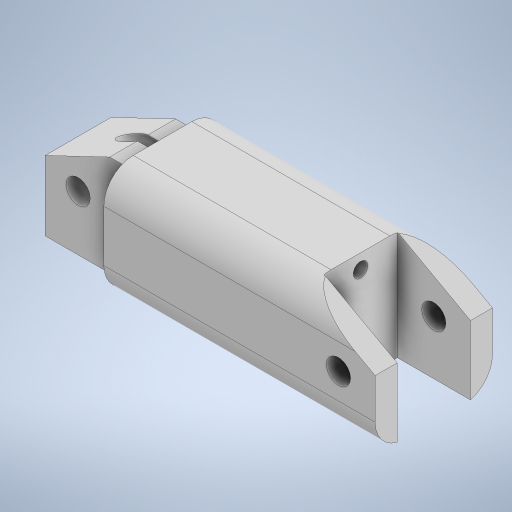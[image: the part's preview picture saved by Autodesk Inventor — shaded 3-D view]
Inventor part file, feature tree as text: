
AUTODESK INVENTOR PART (.ipt)
format: ipt  version: 2024 (Build 280153000, 153)  size: 504,832 bytes
history: native  units: mm
features: sketch x25, extrude x20, chamfer x3, move_body x3, plane x2, split x2, boolean_combine x2, fillet x1
ambient origin geometry x8: Origin, YZ Plane, XZ Plane, XY Plane, X Axis, Y Axis, Z Axis, Center Point
bodies: Solid1 (feature_tree), Solid2 (feature_tree), Solid3 (feature_tree), Solid4 (feature_tree), Solid5 (feature_tree)
feature tree (58):
  extrude  "Extrusion1"  Depth=16.0mm
  sketch  "Sketch2"  dims[d2=15.0mm d3=0.0mm d4=10.0mm]
  extrude  "Extrusion2"  Depth=10.0mm
  chamfer  "Chamfer1"  Distance=21.25mm
  extrude  "Extrusion3"  Depth=10.0mm TaperAngle=0.0deg
  extrude  "Extrusion4"  Depth=11.5mm TaperAngle=0.0deg
  extrude  "Extrusion5"  Depth=1.0mm TaperAngle=0.0deg
  chamfer  "Chamfer2"  Distance=6.0mm Angle=45.0deg
  sketch  "Sketch6"  dims[d14=7.0mm d15=11.5mm d16=0.0mm]
  extrude  "Extrusion6"  Depth=9.0mm
  extrude  "Extrusion7"  Depth=11.5mm TaperAngle=0.0deg
  chamfer  "Chamfer3"  Distance=11.5mm Angle=45.0deg
  sketch  "Sketch9"  dims[d26=3.3mm d27=45.25mm d28=0.0mm d29=11.5mm d30=5.5mm d31=45.0deg]
  extrude  "Extrusion8"  Depth=65.75mm TaperAngle=0.0deg
  extrude  "Extrusion9"  Depth=9.0mm TaperAngle=0.0deg
  extrude  "Extrusion10"  Depth=13.0mm TaperAngle=0.0deg
  sketch  "Sketch13"  dims[d43=24.0mm d44=21.0mm d45=0.0mm]
  extrude  "Extrusion11"  Depth=21.0mm TaperAngle=0.0deg
  extrude  "Extrusion12"  TaperAngle=0.0deg  [1 undecoded]
  extrude  "Extrusion13"  Depth=6.0mm TaperAngle=0.0deg
  plane  "Work Plane1"
  split  "Split1"
  move_body  "Move Body1"
  extrude  "Extrusion14"  Depth=0.5mm TaperAngle=0.0deg
  move_body  "Move Body2"
  fillet  "Fillet1"  Radius=10.0mm
  extrude  "Extrusion15"  Depth=10.0mm TaperAngle=0.0deg
  sketch  "Sketch19"  dims[d71=29.5mm d72=0.0mm d73=13.75mm]
  sketch  "Sketch20"  dims[d74=26.0mm d75=0.0mm d76=-5.0mm d77=0.0mm d78=0.0mm]
  extrude  "Extrusion16"  Depth=1.0mm
  extrude  "Extrusion18"  Depth=13.75mm
  extrude  "Extrusion19"  TaperAngle=0.0deg  [1 undecoded]
  sketch  "Sketch23"
  sketch  "Sketch24"
  extrude  "Extrusion20"  [1 undecoded]
  plane  "Work Plane2"
  boolean_combine  "Combine1"
  split  "Split2"
  extrude  "Extrusion21"  [1 undecoded]
  move_body  "Move Body3"
  boolean_combine  "Combine2"
  sketch  "Sketch1"  dims[d0=36.0mm d1=16.0mm]
  sketch  "Sketch3"  dims[d5=10.0mm]
  sketch  "Sketch4"  dims[d6=3.3mm d7=21.25mm d8=0.0mm]
  sketch  "Sketch5"  dims[d9=10.0mm d10=5.5mm d11=45.0deg d12=10.0mm d13=0.0mm]
  sketch  "Sketch7"  dims[d17=3.3mm d18=1.0mm d19=0.0mm d20=6.0mm d21=11.5mm d22=45.0deg]
  sketch  "Sketch8"  dims[d23=15.0mm d24=0.0mm d25=9.0mm]
  sketch  "Sketch10"  dims[d32=2.0mm d33=65.75mm d34=0.0mm]
  sketch  "Sketch11"  dims[d35=0.5mm d36=0.0mm d37=9.0mm d38=0.0mm]
  sketch  "Sketch12"  dims[d39=0.5mm d40=0.0mm d41=13.0mm d42=0.0mm]
  sketch  "Sketch14"  dims[d46=12.25mm d47=-12.0mm d48=0.0mm d49=0.0mm]
  sketch  "Sketch15"  dims[d50=30.0mm d51=0.0mm d52=6.0mm d53=0.0mm d54=0.0mm d55=4.0mm]
  sketch  "Sketch16"  dims[d56=0.5mm d57=0.0mm d58=0.5mm d59=0.0mm d64=10.0mm d65=0.0mm]
  sketch  "Sketch17"  dims[d66=3.0mm d67=10.0mm d68=0.0mm]
  sketch  "Sketch18"  dims[d69=1.0mm d70=31.0mm]
  sketch  "Sketch22"
  sketch  "Sketch25"
  sketch  "Sketch26"
note: 4 required parameter values undecoded (feature->parameter linkage not recoverable at this tier; creation-order binding heuristic only, values carry confidence <= 0.55)
